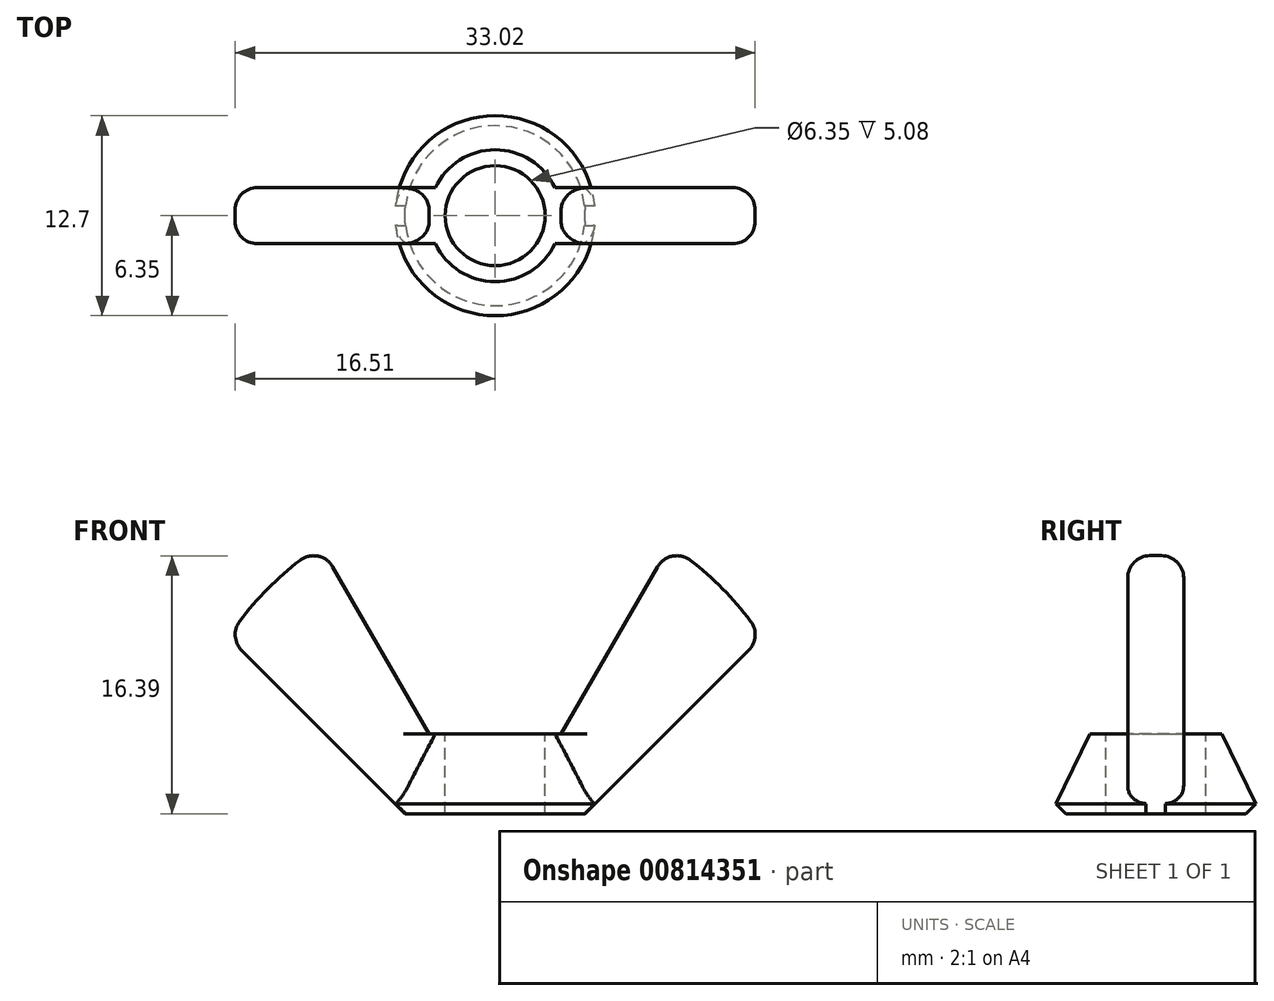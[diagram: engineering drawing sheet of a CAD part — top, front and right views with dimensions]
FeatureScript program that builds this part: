
annotation { "Feature Type Name" : "Feature", "Feature Type Description" : "" }
export const myFeature = defineFeature(function(context is Context, id is Id, definition is map)
    precondition{}
    {
        {
            var Q0;
            Q0=qCreatedBy(makeId("Front.planeOp"),FACE);
            var sketch = newSketch(context, id + "F0", { "sketchPlane" : qUnion([Q0])});
            skLineSegment(sketch, "E0", {"start": v(0, 14.95) * mm, "end": v(0, -15.2) * mm, "construction": true});
            skLineSegment(sketch, "E1", {"start": v(3.18, 0) * mm, "end": v(3.18, 5.08) * mm});
            skLineSegment(sketch, "E2", {"start": v(3.18, 5.08) * mm, "end": v(4.2, 5.08) * mm});
            skLineSegment(sketch, "E3", {"start": v(4.2, 5.08) * mm, "end": v(6.35, 0.64) * mm});
            skLineSegment(sketch, "E4", {"start": v(6.35, 0.64) * mm, "end": v(5.72, 0) * mm});
            skLineSegment(sketch, "E5", {"start": v(5.72, 0) * mm, "end": v(3.18, 0) * mm});
            skSolve(sketch);
        }
        {
            var Q0;
            Q0 = qSketchRegion(id + "F0", true);
            var Q1;
            Q1=sQuery(id+"F0.wireOp",EDGE,"E0");
            revolve(context, id + "F1", {"surfaceOperationType" : NewSurfaceOperationType.NEW, "entities" : qUnion([Q0]), "axis" : qUnion([Q1]), "revolveType" : RevolveType.FULL});
        }
        {
            var Q0;
            Q0=qCreatedBy(makeId("Front.planeOp"),FACE);
            var sketch = newSketch(context, id + "F2", { "sketchPlane" : qUnion([Q0])});
            skLineSegment(sketch, "E6", {"start": v(-6.35, 0.64) * mm, "end": v(-4.2, 5.08) * mm});
            skLineSegment(sketch, "E7", {"start": v(4.2, 5.08) * mm, "end": v(6.35, 0.64) * mm});
            skLineSegment(sketch, "E8", {"start": v(4.2, 5.08) * mm, "end": v(11.09, 17.03) * mm});
            skLineSegment(sketch, "E9", {"start": v(16.94, 11.22) * mm, "end": v(6.35, 0.63) * mm});
            skCircle(sketch, "E10", {"center": v(0, 0) * mm, "radius": 20.32 * mm});
            skLineSegment(sketch, "E11.MirrorCS", {"start": v(-4.2, 5.08) * mm, "end": v(-11.09, 17.03) * mm});
            skLineSegment(sketch, "E12.MirrorCS", {"start": v(-16.94, 11.22) * mm, "end": v(-6.35, 0.63) * mm});
            skLineSegment(sketch, "E13", {"start": v(-5.72, 0) * mm, "end": v(-6.35, 0.64) * mm});
            skLineSegment(sketch, "E14", {"start": v(6.35, 0.64) * mm, "end": v(5.72, 0) * mm});
            skLineSegment(sketch, "E15.0", {"start": v(-5.72, 0) * mm, "end": v(5.72, 0) * mm});
            skLineSegment(sketch, "E16", {"start": v(3.18, 5.08) * mm, "end": v(3.18, 0) * mm});
            skLineSegment(sketch, "E17", {"start": v(-3.18, 0) * mm, "end": v(-3.18, 5.08) * mm});
            skLineSegment(sketch, "E18.0.0", {"start": v(-4.2, 5.08) * mm, "end": v(4.2, 5.08) * mm});
            skSolve(sketch);
        }
        {
            var Q0;
            Q0=makeQuery(id+"F2.imprint","IMPRINT",FACE,{"disambiguationData":[TD([[makeQuery(id+"F2.imprint","IMPRINT",EDGE,{"derivedFrom":sQuery(id+"F2.wireOp",EDGE,"E6")}),1.0]])]});
            var Q1;
            Q1=makeQuery(id+"F2.imprint","IMPRINT",FACE,{"disambiguationData":[TD([[makeQuery(id+"F2.imprint","IMPRINT",EDGE,{"derivedFrom":sQuery(id+"F2.wireOp",EDGE,"E7")}),1.0]])]});
            var Q2;
            {var subQ3=sQuery(id+"F2.wireOp",EDGE,"E6");Q2=makeQuery(id+"F2.imprint","IMPRINT",FACE,{"disambiguationData":[TD([[makeQuery(id+"F2.imprint","IMPRINT",EDGE,{"derivedFrom":subQ3}),-1.0]])]});}
            var Q3;
            {var subQ3=sQuery(id+"F2.wireOp",EDGE,"E7");Q3=makeQuery(id+"F2.imprint","IMPRINT",FACE,{"disambiguationData":[TD([[makeQuery(id+"F2.imprint","IMPRINT",EDGE,{"derivedFrom":subQ3}),-1.0]])]});}
            extrude(context, id + "F3", {"entities" : qUnion([Q0, Q1, Q2, Q3]), "operationType" : NewBodyOperationType.ADD, "depth" : 3.56 * mm, "offsetDistance" : 25.4 * mm, "symmetric" : true});
        }
        {
            var Q0;
            Q0=makeQuery(id+"F3.opExtrude","CAP_EDGE",EDGE,{"disambiguationData":[OSD([sQuery(id+"F2.wireOp",EDGE,"E11.MirrorCS")])],"isStart":false});
            var Q1;
            Q1=makeQuery(id+"F3.opExtrude","CAP_EDGE",EDGE,{"disambiguationData":[OSD([sQuery(id+"F2.wireOp",EDGE,"E12.MirrorCS"),sQuery(id+"F2.wireOp",EDGE,"E13")])],"isStart":false});
            var Q2;
            Q2=makeQuery(id+"F3.opExtrude","CAP_EDGE",EDGE,{"disambiguationData":[OSD([sQuery(id+"F2.wireOp",EDGE,"E12.MirrorCS"),sQuery(id+"F2.wireOp",EDGE,"E13")])],"isStart":true});
            var Q3;
            Q3=makeQuery(id+"F3.opExtrude","CAP_EDGE",EDGE,{"disambiguationData":[OSD([sQuery(id+"F2.wireOp",EDGE,"E11.MirrorCS")])],"isStart":true});
            var Q4;
            {var subQ0=sQuery(id+"F2.wireOp",EDGE,"E10");Q4=makeQuery(id+"F3.opExtrude","SWEPT_FACE",FACE,{"disambiguationData":[OSD([subQ0]),TDD([makeQuery(id+"F2.imprint","IMPRINT",EDGE,{"disambiguationData":[TD([[makeQuery(id+"F2.imprint","INTERSECT",VERTEX,{"derivedFrom":[subQ0,sQuery(id+"F2.wireOp",EDGE,"E11.MirrorCS")]}),-1.0]])],"derivedFrom":subQ0})])]});}
            var Q5;
            Q5=makeQuery(id+"F3.opExtrude","CAP_EDGE",EDGE,{"disambiguationData":[OSD([sQuery(id+"F2.wireOp",EDGE,"E9"),sQuery(id+"F2.wireOp",EDGE,"E14")])],"isStart":true});
            var Q6;
            Q6=makeQuery(id+"F3.opExtrude","CAP_EDGE",EDGE,{"disambiguationData":[OSD([sQuery(id+"F2.wireOp",EDGE,"E9"),sQuery(id+"F2.wireOp",EDGE,"E14")])],"isStart":false});
            var Q7;
            {var subQ0=sQuery(id+"F2.wireOp",EDGE,"E10");Q7=makeQuery(id+"F3.opExtrude","SWEPT_FACE",FACE,{"disambiguationData":[OSD([subQ0]),TDD([makeQuery(id+"F2.imprint","IMPRINT",EDGE,{"disambiguationData":[TD([[makeQuery(id+"F2.imprint","INTERSECT",VERTEX,{"derivedFrom":[sQuery(id+"F2.wireOp",EDGE,"E8"),subQ0]}),1.0]])],"derivedFrom":subQ0})])]});}
            var Q8;
            Q8=makeQuery(id+"F3.opExtrude","CAP_EDGE",EDGE,{"disambiguationData":[OSD([sQuery(id+"F2.wireOp",EDGE,"E8")])],"isStart":true});
            var Q9;
            Q9=makeQuery(id+"F3.opExtrude","CAP_EDGE",EDGE,{"disambiguationData":[OSD([sQuery(id+"F2.wireOp",EDGE,"E8")])],"isStart":false});
            fillet(context, id + "F4", {"entities" : qUnion([Q0, Q1, Q2, Q3, Q4, Q5, Q6, Q7, Q8, Q9]), "radius" : 1.41 * mm, "tangentPropagation" : true, "allowEdgeOverflow" : false});
        }
    });
